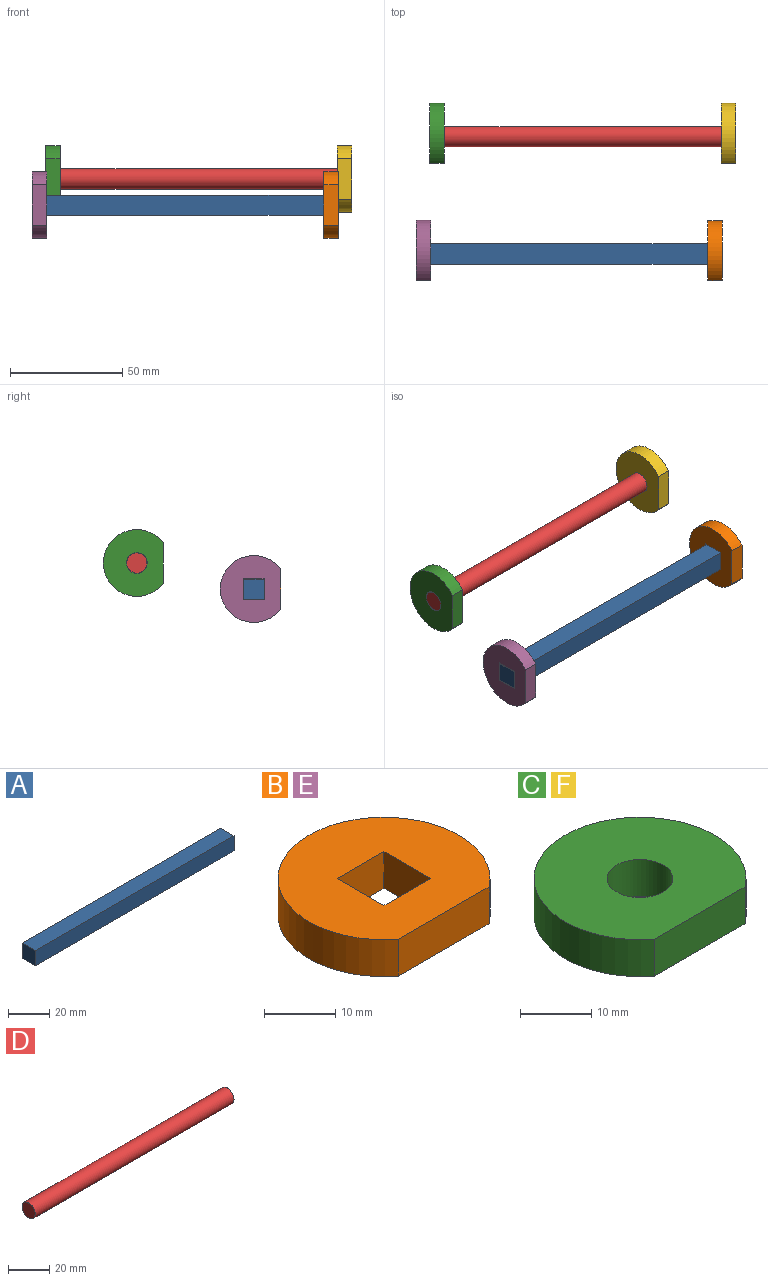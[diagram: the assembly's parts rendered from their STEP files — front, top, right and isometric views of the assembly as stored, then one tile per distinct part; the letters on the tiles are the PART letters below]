
ASSEMBLY  parts=6 mates=10
PART A: 6 faces, bbox 136.4x9x9 mm
  f0: plane 136.35x9mm, normal (0,-1,0), area 1227.1mm2, adj f1,f3,f4,f5
  f1: plane 136.35x9mm, normal (0,0,-1), area 1227.1mm2, adj f0,f2,f4,f5
  f2: plane 136.35x9mm, normal (0,1,0), area 1227.1mm2, adj f1,f3,f4,f5
  f3: plane 136.35x9mm, normal (0,0,1), area 1227.1mm2, adj f0,f2,f4,f5
  f4: plane 9x9mm, normal (1,0,0), area 81mm2, adj f0,f1,f2,f3
  f5: plane 9x9mm, normal (-1,0,0), area 81mm2, adj f0,f1,f2,f3
PART B: 8 faces, bbox 29.8x26.8x6.4 mm
  f0: plane 9.3x6.35mm, normal (0,-1,0), area 59.1mm2, adj f1,f5,f6,f7
  f1: plane 9.3x6.35mm, normal (-1,0,0), area 59.1mm2, adj f0,f2,f6,f7
  f2: plane 9.3x6.35mm, normal (0,1,0), area 59.1mm2, adj f1,f5,f6,f7
  f3: cylinder r=14.9mm len=29.8mm, axis (0,0,-1), area 471.8mm2, adj f4,f6,f7
  f4: plane 18x6.35mm, normal (0,-1,0), area 114.3mm2, adj f3,f6,f7
  f5: plane 9.3x6.35mm, normal (1,0,0), area 59.1mm2, adj f0,f2,f6,f7
  f6: plane 29.8x26.77mm, normal (0,0,1), area 573.9mm2, adj f0,f1,f2,f3,f4,f5
  f7: plane 29.8x26.77mm, normal (0,0,-1), area 573.9mm2, adj f0,f1,f2,f3,f4,f5
PART C: 5 faces, bbox 29.8x26.8x6.4 mm
  f0: cylinder r=14.9mm len=29.8mm, axis (0,0,-1), area 471.8mm2, adj f2,f3,f4
  f1: cylinder r=4.62mm len=9.25mm, axis (0,0,-1), area 184.5mm2, adj f3,f4
  f2: plane 18x6.35mm, normal (0,-1,0), area 114.3mm2, adj f0,f3,f4
  f3: plane 29.8x26.77mm, normal (0,0,1), area 593.2mm2, adj f0,f1,f2
  f4: plane 29.8x26.77mm, normal (0,0,-1), area 593.2mm2, adj f0,f1,f2
PART D: 3 faces, bbox 136.4x9x9 mm
  f0: cylinder r=4.5mm len=136.35mm, axis (-1,0,0), area 3855.2mm2, adj f1,f2
  f1: plane 9x9mm, normal (1,0,0), area 63.6mm2, adj f0
  f2: plane 9x9mm, normal (-1,0,0), area 63.6mm2, adj f0
PART E: same geometry as B
PART F: same geometry as C
PLACE A t=(-13.89,25.6,-2.31)mm fixed
PLACE B rot(axis=(0,-1,0),90deg) t=(122.46,30.1,2.34)mm
PLACE C rot(axis=(0,1,0),90deg) t=(-7.93,82.38,13.94)mm
PLACE D t=(-7.93,82.38,13.94)mm fixed
PLACE E rot(axis=(0,1,0),90deg) t=(-13.89,30.25,2.34)mm
PLACE F rot(axis=(0,-1,0),90deg) t=(128.42,82.38,13.94)mm
MATE planar D.f0 <-> F.f4  axis (1,0,0) through (128.42,82.38,13.94)mm
MATE planar E.f7 <-> A.f5  axis (-1,0,0) through (-13.89,34.9,6.99)mm
MATE planar E.f1 <-> A.f1  axis (0,0,1) through (-10.72,30.25,-2.31)mm
MATE planar C.f4 <-> D.f0  axis (-1,0,0) through (-7.93,83.2,13.94)mm
MATE planar F.f2 <-> C.f2  axis (0,-1,0) through (125.24,70.5,13.94)mm
MATE planar B.f7 <-> A.f4  axis (1,0,0) through (122.46,34.75,6.99)mm
MATE planar E.f2 <-> A.f0  axis (0,1,0) through (-7.54,25.6,6.99)mm
MATE cylindrical D.f0 <-> C.f1  axis (-1,0,0) through (60.24,82.38,13.94)mm
MATE planar A.f1 <-> B.f5  axis (0,0,-1) through (54.28,30.1,-2.31)mm
MATE cylindrical D.f0 <-> F.f1  axis (-1,0,0) through (60.24,82.38,13.94)mm
